# Revit family: result
name_source: partatom
category: Specialty Equipment
revit_build: Autodesk Revit 2015 (Build: 20140903_1530(x64)
units: mm (PartAtom-declared; Revit-internal decimal feet)

## types (1)
- Default
    BIMobject category = Dispensers
    BIMobject category code = sanitary-dispensers
    BIMobject main category = Sanitary
    BIMobject main category code = sanitary
    Brand url = http://www.delabie.com
    Design country = France
    Edition number = 1
    GTIN code = https://3456330016469
    IFC Classification = Furnishing Element
    Installation instructions = https://www.delabie.com
    Manufacturer country = France
    Manufacturer name = DELABIE
    OmniClass Code = 23-31 25 29 13
    OmniClass Description = Hand Soap Dispensers
    Product Guid = b9c6e284-c1bb-436c-b591-68aaed2745f8
    Product SKU = 729012
    Product data url = https://bimobject.com
    Product family = Sanitary
    Product group = Accessories
    Product name = 729012 Liquid soap dispenser - curved spout - 1L
    Product url = https://www.delabie.com
    QR code = http://bimobject.com
    Technical description = https://www.delabie.com
    UNSPSC Code = 301815
    Uniclass 2015 Code = Pr_40_20_76
    Uniclass 2015 Name = Sanitary accessories

## geometry (parser evidence)
native form markers: Sweep x3
no freeform markers — native parametric forms only
